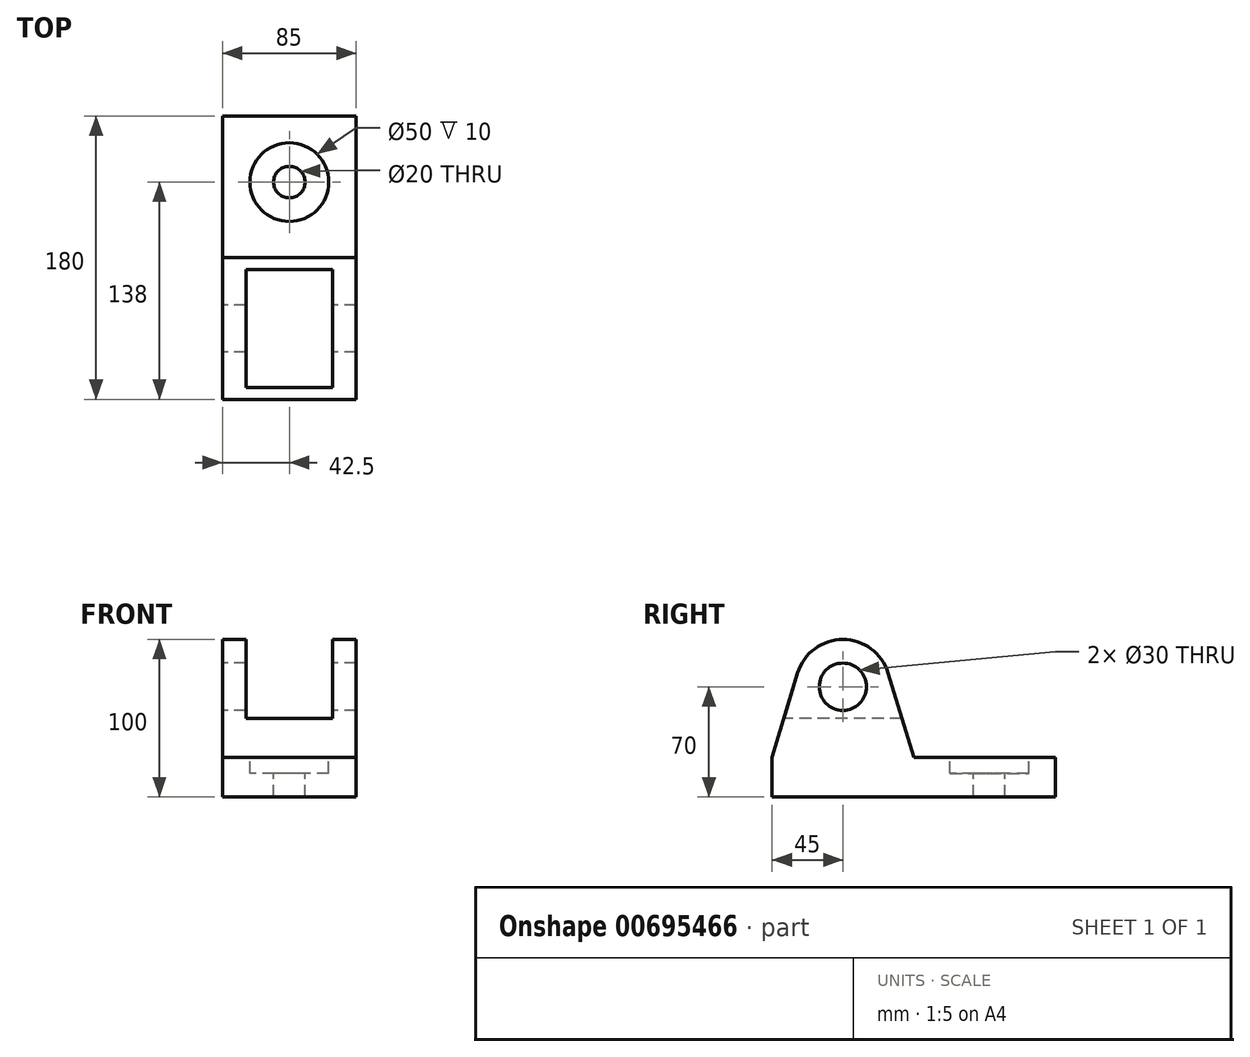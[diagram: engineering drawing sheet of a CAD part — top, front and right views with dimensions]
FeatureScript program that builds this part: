
annotation { "Feature Type Name" : "Feature", "Feature Type Description" : "" }
export const myFeature = defineFeature(function(context is Context, id is Id, definition is map)
    precondition{}
    {
        {
            var Q0;
            Q0=qCreatedBy(makeId("Top.planeOp"),FACE);
            var sketch = newSketch(context, id + "F0", { "sketchPlane" : qUnion([Q0])});
            skLineSegment(sketch, "E0.bottom", {"start": v(-42.5, 90) * mm, "end": v(42.5, 90) * mm});
            skLineSegment(sketch, "E0.top", {"start": v(-42.5, -90) * mm, "end": v(42.5, -90) * mm});
            skLineSegment(sketch, "E0.left", {"start": v(-42.5, 90) * mm, "end": v(-42.5, -90) * mm});
            skLineSegment(sketch, "E0.right", {"start": v(42.5, 90) * mm, "end": v(42.5, -90) * mm});
            skPoint(sketch, "E0.middle", {"position": v(0, 0) * mm});
            skSolve(sketch);
        }
        {
            var Q0;
            Q0=makeQuery(id+"F0.imprint","IMPRINT",FACE,{"disambiguationData":[TD([[makeQuery(id+"F0.imprint","IMPRINT",EDGE,{"derivedFrom":sQuery(id+"F0.wireOp",EDGE,"E0.bottom")}),-1.0]])]});
            extrude(context, id + "F1", {"entities" : qUnion([Q0]), "depth" : 25 * mm, "offsetDistance" : 25 * mm});
        }
        {
            var Q0;
            Q0=qCreatedBy(makeId("Right.planeOp"),FACE);
            var sketch = newSketch(context, id + "F2", { "sketchPlane" : qUnion([Q0])});
            skCircle(sketch, "E1", {"center": v(-45, 70) * mm, "radius": 15 * mm});
            skArc(sketch, "E2", {"start": v(-16.3, 78.7) * mm, "mid": v(-45, 100) * mm, "end": v(-73.7, 78.7) * mm});
            skPoint(sketch, "E3.0", {"position": v(-90, 25) * mm});
            skLineSegment(sketch, "E4", {"start": v(-90, 25) * mm, "end": v(-73.7, 78.7) * mm});
            skLineSegment(sketch, "E5", {"start": v(-90, 25) * mm, "end": v(0, 25) * mm});
            skLineSegment(sketch, "E6", {"start": v(0, 25) * mm, "end": v(-16.3, 78.7) * mm});
            skLineSegment(sketch, "E7", {"start": v(15.13, 50) * mm, "end": v(-111.12, 50) * mm, "construction": true});
            skSolve(sketch);
        }
        {
            var Q0;
            Q0=makeQuery(id+"F2.imprint","IMPRINT",FACE,{"disambiguationData":[TD([[makeQuery(id+"F2.imprint","IMPRINT",EDGE,{"derivedFrom":sQuery(id+"F2.wireOp",EDGE,"E1")}),-1.0]])]});
            var Q1;
            Q1=makeQuery(id+"F1.opExtrude","SWEPT_FACE",FACE,{"disambiguationData":[OSD([sQuery(id+"F0.wireOp",EDGE,"E0.right")])]});
            var Q2;
            Q2=makeQuery(id+"F1.opExtrude","SWEPT_FACE",FACE,{"disambiguationData":[OSD([sQuery(id+"F0.wireOp",EDGE,"E0.left")])]});
            extrude(context, id + "F3", {"entities" : qUnion([Q0]), "operationType" : NewBodyOperationType.ADD, "endBound" : BoundingType.UP_TO_SURFACE, "depth" : 25 * mm, "endBoundEntityFace" : qUnion([Q1]), "offsetDistance" : 25 * mm, "hasSecondDirection" : true, "secondDirectionBound" : BoundingType.UP_TO_SURFACE, "secondDirectionOppositeDirection" : true, "secondDirectionDepth" : 25 * mm, "secondDirectionBoundEntityFace" : qUnion([Q2])});
        }
        {
            var Q0;
            Q0=makeQuery(id+"F1.opExtrude","SWEPT_FACE",FACE,{"disambiguationData":[OSD([sQuery(id+"F0.wireOp",EDGE,"E0.top")])]});
            var sketch = newSketch(context, id + "F4", { "sketchPlane" : qUnion([Q0])});
            skLineSegment(sketch, "E8.bottom", {"start": v(-27.5, 50) * mm, "end": v(27.5, 50) * mm});
            skLineSegment(sketch, "E8.top", {"start": v(-27.5, 115) * mm, "end": v(27.5, 115) * mm});
            skLineSegment(sketch, "E8.left", {"start": v(-27.5, 50) * mm, "end": v(-27.5, 115) * mm});
            skLineSegment(sketch, "E8.right", {"start": v(27.5, 50) * mm, "end": v(27.5, 115) * mm});
            skSolve(sketch);
        }
        {
            var Q0;
            Q0=makeQuery(id+"F4.imprint","IMPRINT",FACE,{"disambiguationData":[TD([[makeQuery(id+"F4.imprint","IMPRINT",EDGE,{"derivedFrom":sQuery(id+"F4.wireOp",EDGE,"E8.bottom")}),1.0]])]});
            extrude(context, id + "F5", {"entities" : qUnion([Q0]), "operationType" : NewBodyOperationType.REMOVE, "endBound" : BoundingType.THROUGH_ALL, "oppositeDirection" : true, "depth" : 25 * mm, "offsetDistance" : 25 * mm});
        }
        {
            var Q0;
            Q0=makeQuery(id+"F1.opExtrude","CAP_FACE",FACE,{"disambiguationData":[OSD([sQuery(id+"F0.wireOp",EDGE,"E0.bottom"),sQuery(id+"F0.wireOp",EDGE,"E0.top"),sQuery(id+"F0.wireOp",EDGE,"E0.left"),sQuery(id+"F0.wireOp",EDGE,"E0.right")])],"isStart":false});
            var sketch = newSketch(context, id + "F6", { "sketchPlane" : qUnion([Q0])});
            skCircle(sketch, "E9", {"center": v(0, 48) * mm, "radius": 25 * mm});
            skSolve(sketch);
        }
        {
            var Q0;
            Q0=makeQuery(id+"F6.imprint","IMPRINT",FACE,{"disambiguationData":[TD([[makeQuery(id+"F6.imprint","IMPRINT",EDGE,{"derivedFrom":sQuery(id+"F6.wireOp",EDGE,"E9")}),1.0]])]});
            extrude(context, id + "F7", {"entities" : qUnion([Q0]), "operationType" : NewBodyOperationType.REMOVE, "oppositeDirection" : true, "depth" : 10 * mm, "offsetDistance" : 25 * mm});
        }
        {
            var Q0;
            Q0=makeQuery(id+"F7.boolean.opBoolean","COPY",FACE,{"derivedFrom":makeQuery(id+"F7.opExtrude","CAP_FACE",FACE,{"disambiguationData":[OSD([sQuery(id+"F6.wireOp",EDGE,"E9")])],"isStart":false})});
            var sketch = newSketch(context, id + "F8", { "sketchPlane" : qUnion([Q0])});
            skCircle(sketch, "E10", {"center": v(0, 48) * mm, "radius": 10 * mm});
            skSolve(sketch);
        }
        {
            var Q0;
            Q0=makeQuery(id+"F8.imprint","IMPRINT",FACE,{"disambiguationData":[TD([[makeQuery(id+"F8.imprint","IMPRINT",EDGE,{"derivedFrom":sQuery(id+"F8.wireOp",EDGE,"E10")}),1.0]])]});
            extrude(context, id + "F9", {"entities" : qUnion([Q0]), "operationType" : NewBodyOperationType.REMOVE, "endBound" : BoundingType.THROUGH_ALL, "oppositeDirection" : true, "depth" : 25 * mm, "offsetDistance" : 25 * mm});
        }
    });
